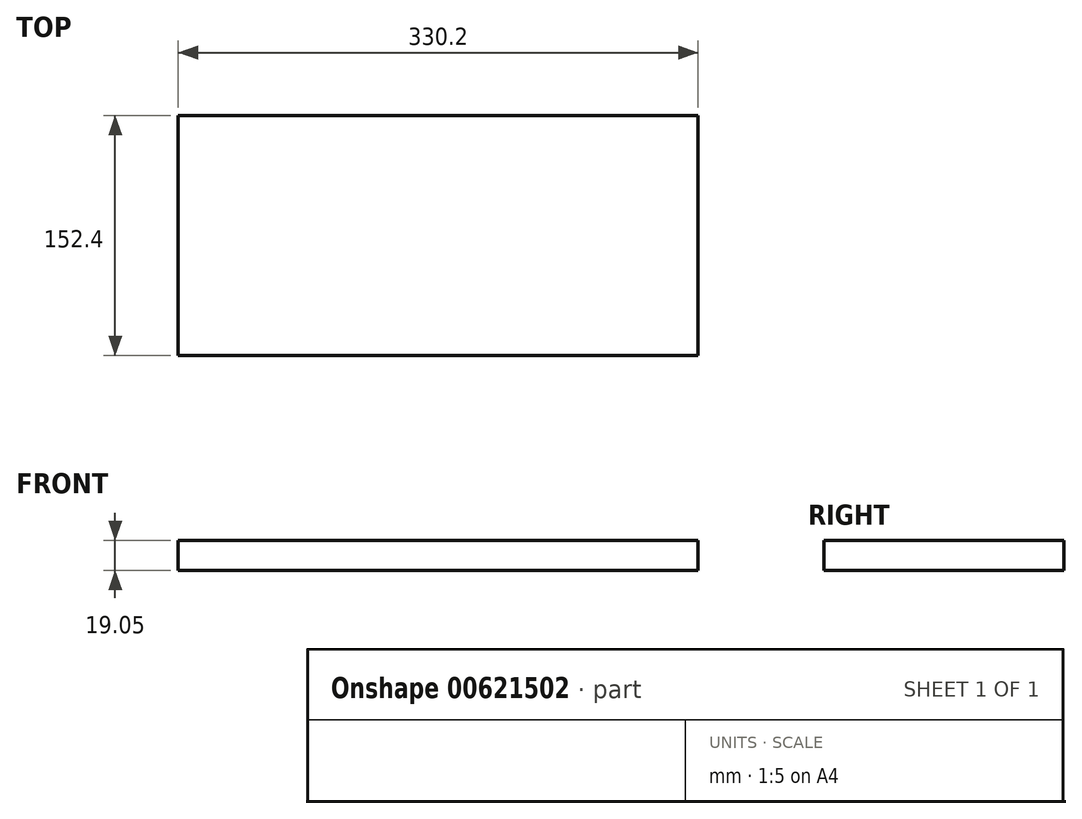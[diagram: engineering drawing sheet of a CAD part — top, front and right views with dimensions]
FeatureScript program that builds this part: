
annotation { "Feature Type Name" : "Feature", "Feature Type Description" : "" }
export const myFeature = defineFeature(function(context is Context, id is Id, definition is map)
    precondition{}
    {
        {
            var Q0;
            Q0=qCreatedBy(makeId("Top.planeOp"),FACE);
            var sketch = newSketch(context, id + "F0", { "sketchPlane" : qUnion([Q0])});
            skLineSegment(sketch, "E0.bottom", {"start": v(0, 0) * mm, "end": v(279.4, 0) * mm});
            skLineSegment(sketch, "E0.top", {"start": v(0, 152.4) * mm, "end": v(279.4, 152.4) * mm});
            skLineSegment(sketch, "E0.left", {"start": v(0, 0) * mm, "end": v(0, 152.4) * mm});
            skLineSegment(sketch, "E0.right", {"start": v(279.4, 0) * mm, "end": v(279.4, 152.4) * mm});
            skLineSegment(sketch, "E1.bottom", {"start": v(0, 152.4) * mm, "end": v(-50.8, 152.4) * mm});
            skLineSegment(sketch, "E1.top", {"start": v(0, 0) * mm, "end": v(-50.8, 0) * mm});
            skLineSegment(sketch, "E1.left", {"start": v(0, 152.4) * mm, "end": v(0, 0) * mm});
            skLineSegment(sketch, "E1.right", {"start": v(-50.8, 152.4) * mm, "end": v(-50.8, 0) * mm});
            skSolve(sketch);
        }
        {
            var Q0;
            Q0=makeQuery(id+"F0.imprint","IMPRINT",FACE,{"disambiguationData":[TD([[makeQuery(id+"F0.imprint","IMPRINT",EDGE,{"derivedFrom":sQuery(id+"F0.wireOp",EDGE,"E0.bottom")}),1.0]])]});
            var Q1;
            Q1=makeQuery(id+"F0.imprint","IMPRINT",FACE,{"disambiguationData":[TD([[makeQuery(id+"F0.imprint","IMPRINT",EDGE,{"derivedFrom":sQuery(id+"F0.wireOp",EDGE,"E1.bottom")}),1.0]])]});
            extrude(context, id + "F1", {"entities" : qUnion([Q0, Q1]), "depth" : 19.05 * mm, "offsetDistance" : 25.4 * mm});
        }
    });
